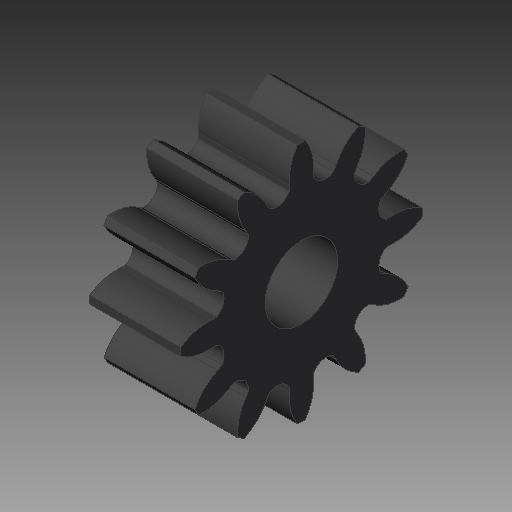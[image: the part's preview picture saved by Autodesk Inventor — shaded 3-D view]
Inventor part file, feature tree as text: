
AUTODESK INVENTOR PART (.ipt)
format: ipt  version: 2018 (Build 220112000, 112)  size: 294,912 bytes
history: native  units: in
note: dims shown in document units (in); Inventor stores cm internally (conversion verified against a paired STEP export)
features: extrude x3, sketch x3, plane x1
ambient origin geometry x8: Origin, YZ Plane, XZ Plane, XY Plane, X Axis, Y Axis, Z Axis, Center Point
bodies: Solid1 (feature_tree)
feature tree (7):
  plane  "Work Plane2"
  extrude  "Extrusion19"  Depth=0.2255in TaperAngle=0.0deg
  extrude  "Extrusion20"  Depth=100.0in TaperAngle=0.0deg
  extrude  "Extrusion21"  Depth=4.7244in TaperAngle=360.0deg
  sketch  "Sketch6"  dims[d92=4.7244in d94=360.0deg d102=0.2255in d103=0.0in]
  sketch  "Sketch7"  dims[d104=0.18in d105=100.0in d106=0.0in]
  sketch  "Sketch8"  dims[d107=0.4in d108=4.7244in d110=360.0deg d112=100.0in d113=0.0in]
